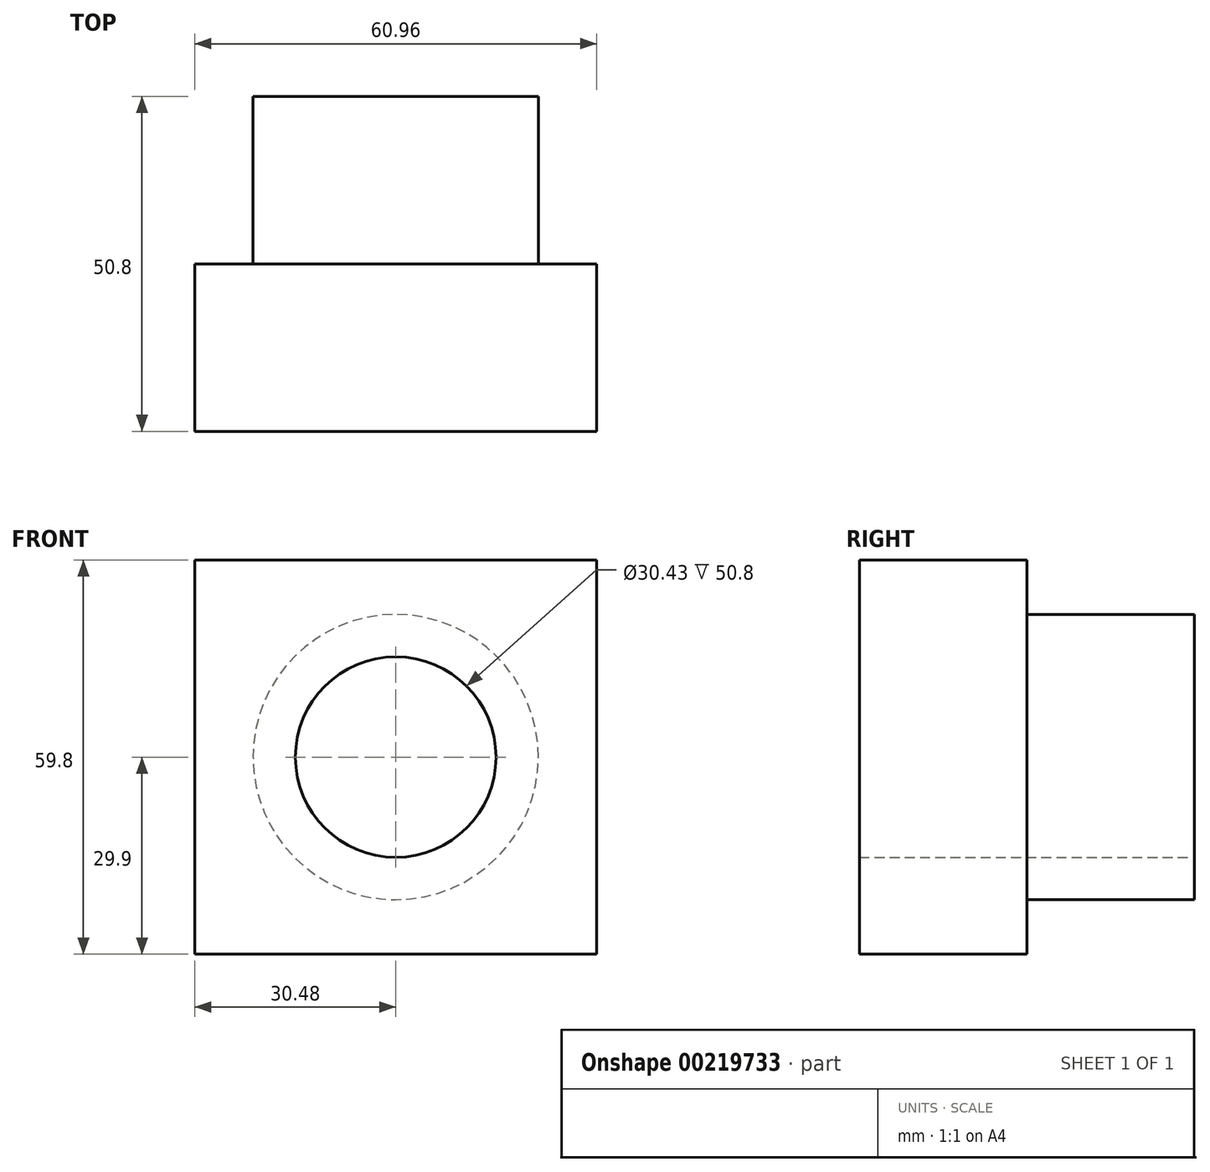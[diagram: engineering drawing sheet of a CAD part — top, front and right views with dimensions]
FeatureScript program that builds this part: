
annotation { "Feature Type Name" : "Feature", "Feature Type Description" : "" }
export const myFeature = defineFeature(function(context is Context, id is Id, definition is map)
    precondition{}
    {
        {
            var Q0;
            Q0=qCreatedBy(makeId("Front.planeOp"),FACE);
            var sketch = newSketch(context, id + "F0", { "sketchPlane" : qUnion([Q0])});
            skLineSegment(sketch, "E0.bottom", {"start": v(30.48, -29.9) * mm, "end": v(-30.48, -29.9) * mm});
            skLineSegment(sketch, "E0.top", {"start": v(30.48, 29.9) * mm, "end": v(-30.48, 29.9) * mm});
            skLineSegment(sketch, "E0.left", {"start": v(30.48, -29.9) * mm, "end": v(30.48, 29.9) * mm});
            skLineSegment(sketch, "E0.right", {"start": v(-30.48, -29.9) * mm, "end": v(-30.48, 29.9) * mm});
            skPoint(sketch, "E0.middle", {"position": v(0, 0) * mm});
            skSolve(sketch);
        }
        {
            var Q0;
            Q0=makeQuery(id+"F0.imprint","IMPRINT",FACE,{"disambiguationData":[TD([[makeQuery(id+"F0.imprint","IMPRINT",EDGE,{"derivedFrom":sQuery(id+"F0.wireOp",EDGE,"E0.bottom")}),-1.0]])]});
            extrude(context, id + "F1", {"entities" : qUnion([Q0]), "depth" : 25.4 * mm});
        }
        {
            var Q0;
            Q0=qCreatedBy(makeId("Front.planeOp"),FACE);
            var sketch = newSketch(context, id + "F2", { "sketchPlane" : qUnion([Q0])});
            skCircle(sketch, "E1", {"center": v(0, 0) * mm, "radius": 21.63 * mm});
            skCircle(sketch, "E2", {"center": v(0, 0) * mm, "radius": 15.21 * mm});
            skSolve(sketch);
        }
        {
            var Q0;
            Q0=makeQuery(id+"F2.imprint","IMPRINT",FACE,{"disambiguationData":[TD([[makeQuery(id+"F2.imprint","IMPRINT",EDGE,{"derivedFrom":sQuery(id+"F2.wireOp",EDGE,"E1")}),1.0]])]});
            extrude(context, id + "F3", {"entities" : qUnion([Q0]), "operationType" : NewBodyOperationType.ADD, "endBound" : BoundingType.SYMMETRIC, "depth" : 50.8 * mm});
        }
        {
            var Q0;
            Q0=makeQuery(id+"F3.boolean.opBoolean","SPLIT",FACE,{"disambiguationData":[TD([makeQuery(id+"F3.opExtrude","SWEPT_FACE",FACE,{"disambiguationData":[OSD([sQuery(id+"F2.wireOp",EDGE,"E2")])]})])],"derivedFrom":makeQuery(id+"F1.opExtrude","CAP_FACE",FACE,{"disambiguationData":[OSD([sQuery(id+"F0.wireOp",EDGE,"E0.bottom"),sQuery(id+"F0.wireOp",EDGE,"E0.top"),sQuery(id+"F0.wireOp",EDGE,"E0.left"),sQuery(id+"F0.wireOp",EDGE,"E0.right")])],"isStart":true})});
            extrude(context, id + "F4", {"entities" : qUnion([Q0]), "operationType" : NewBodyOperationType.REMOVE, "oppositeDirection" : true, "depth" : 25.4 * mm});
        }
    });
